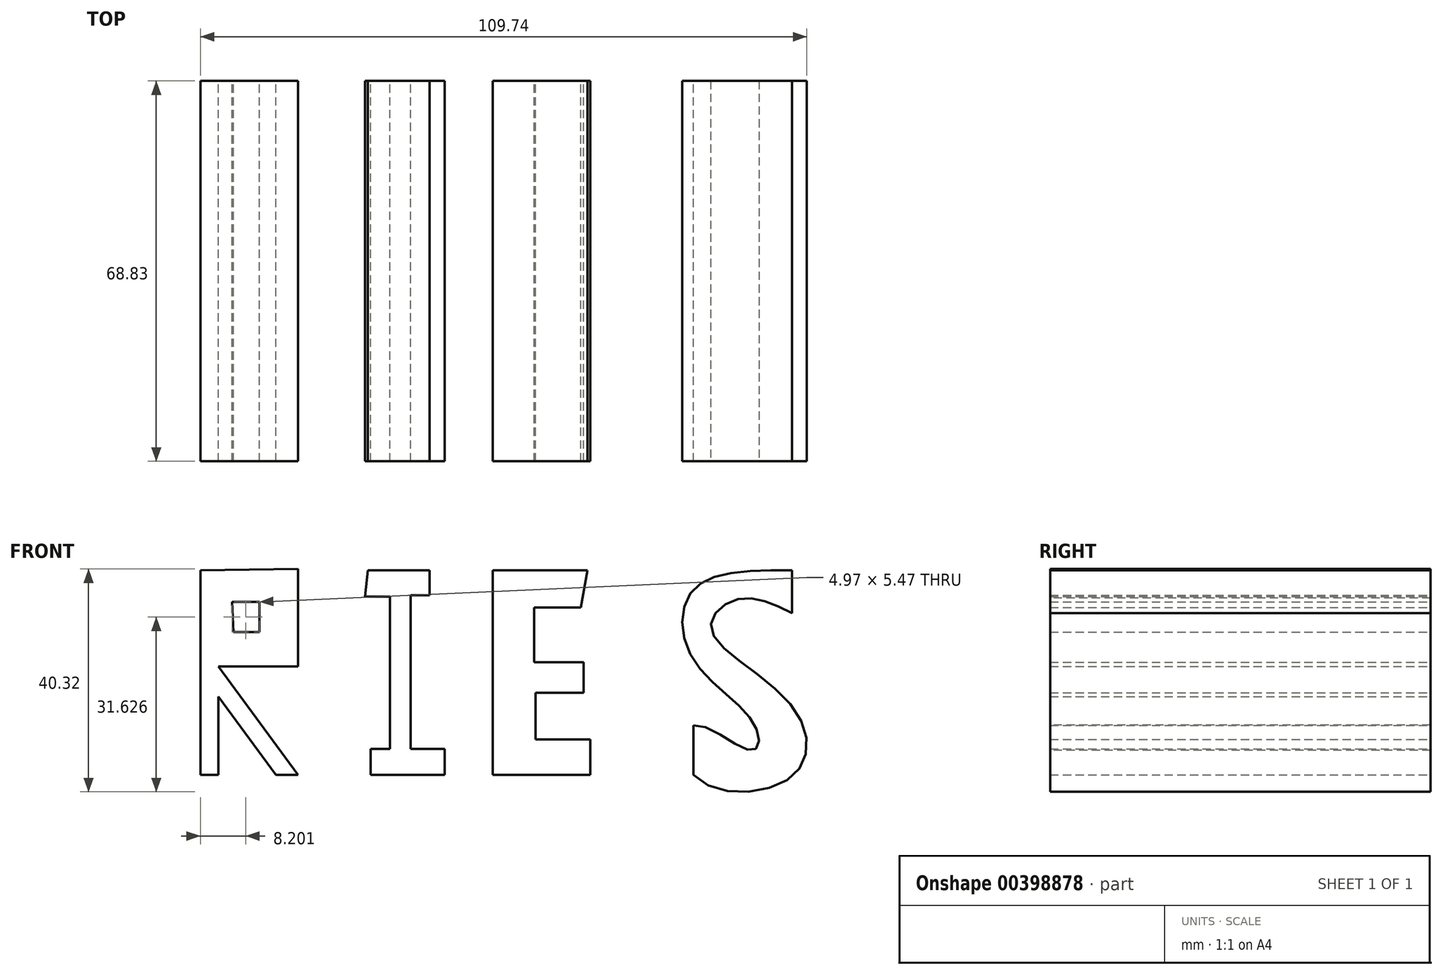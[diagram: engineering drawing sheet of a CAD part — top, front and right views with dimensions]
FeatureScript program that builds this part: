
annotation { "Feature Type Name" : "Feature", "Feature Type Description" : "" }
export const myFeature = defineFeature(function(context is Context, id is Id, definition is map)
    precondition{}
    {
        {
            var Q0;
            Q0=qCreatedBy(makeId("Front.planeOp"),FACE);
            var sketch = newSketch(context, id + "F0", { "sketchPlane" : qUnion([Q0])});
            skLineSegment(sketch, "E0", {"start": v(-44.23, 49.94) * mm, "end": v(-44.23, 12.92) * mm});
            skLineSegment(sketch, "E1", {"start": v(-44.23, 12.92) * mm, "end": v(-41, 12.92) * mm});
            skLineSegment(sketch, "E2", {"start": v(-41, 12.92) * mm, "end": v(-41, 27.08) * mm});
            skLineSegment(sketch, "E3", {"start": v(-41, 27.08) * mm, "end": v(-30.56, 12.92) * mm});
            skLineSegment(sketch, "E4", {"start": v(-30.56, 12.92) * mm, "end": v(-26.59, 12.92) * mm});
            skLineSegment(sketch, "E5", {"start": v(-26.59, 12.92) * mm, "end": v(-41, 32.55) * mm});
            skLineSegment(sketch, "E6", {"start": v(-41, 32.55) * mm, "end": v(-26.59, 32.55) * mm});
            skLineSegment(sketch, "E7", {"start": v(-26.59, 32.55) * mm, "end": v(-26.59, 50.2) * mm});
            skLineSegment(sketch, "E8", {"start": v(-26.59, 50.2) * mm, "end": v(-44.23, 49.94) * mm});
            skLineSegment(sketch, "E9", {"start": v(-13.91, 49.94) * mm, "end": v(-2.73, 49.94) * mm});
            skLineSegment(sketch, "E10", {"start": v(-2.73, 49.94) * mm, "end": v(-2.73, 45.47) * mm});
            skLineSegment(sketch, "E11", {"start": v(-2.73, 45.47) * mm, "end": v(-6.21, 45.47) * mm});
            skLineSegment(sketch, "E12", {"start": v(-6.21, 45.47) * mm, "end": v(-6.21, 17.64) * mm});
            skLineSegment(sketch, "E13", {"start": v(-6.21, 17.64) * mm, "end": v(0, 17.64) * mm});
            skLineSegment(sketch, "E14", {"start": v(0, 17.64) * mm, "end": v(0, 12.92) * mm});
            skLineSegment(sketch, "E15", {"start": v(0, 12.92) * mm, "end": v(-13.42, 12.92) * mm});
            skLineSegment(sketch, "E16", {"start": v(-13.42, 12.92) * mm, "end": v(-13.42, 17.64) * mm});
            skLineSegment(sketch, "E17", {"start": v(-13.42, 17.64) * mm, "end": v(-9.94, 17.64) * mm});
            skLineSegment(sketch, "E18", {"start": v(-9.94, 17.64) * mm, "end": v(-9.94, 45.22) * mm});
            skLineSegment(sketch, "E19", {"start": v(-9.94, 45.22) * mm, "end": v(-14.41, 45.22) * mm});
            skLineSegment(sketch, "E20", {"start": v(-14.41, 45.22) * mm, "end": v(-13.91, 49.94) * mm});
            skLineSegment(sketch, "E21", {"start": v(25.84, 49.94) * mm, "end": v(8.7, 49.94) * mm});
            skLineSegment(sketch, "E22", {"start": v(8.7, 49.94) * mm, "end": v(8.7, 12.92) * mm});
            skLineSegment(sketch, "E23", {"start": v(8.7, 12.92) * mm, "end": v(26.34, 12.92) * mm});
            skLineSegment(sketch, "E24", {"start": v(26.34, 12.92) * mm, "end": v(26.34, 19.38) * mm});
            skLineSegment(sketch, "E25", {"start": v(26.34, 19.38) * mm, "end": v(16.4, 19.38) * mm});
            skLineSegment(sketch, "E26", {"start": v(16.4, 19.38) * mm, "end": v(16.4, 27.83) * mm});
            skLineSegment(sketch, "E27", {"start": v(16.4, 27.83) * mm, "end": v(25.1, 27.83) * mm});
            skLineSegment(sketch, "E28", {"start": v(25.1, 27.83) * mm, "end": v(25.1, 33.3) * mm});
            skLineSegment(sketch, "E29", {"start": v(25.1, 33.3) * mm, "end": v(16.15, 33.3) * mm});
            skLineSegment(sketch, "E30", {"start": v(16.15, 33.3) * mm, "end": v(16.15, 43.24) * mm});
            skLineSegment(sketch, "E31", {"start": v(16.15, 43.24) * mm, "end": v(24.6, 43.24) * mm});
            skLineSegment(sketch, "E32", {"start": v(24.6, 43.24) * mm, "end": v(25.84, 49.94) * mm});
            skLineSegment(sketch, "E33", {"start": v(62.87, 49.94) * mm, "end": v(62.87, 42.24) * mm});
            skLineSegment(sketch, "E34", {"start": v(44.97, 21.87) * mm, "end": v(44.97, 12.92) * mm});
            skPoint(sketch, "E35.7.internal.snap0", {"position": v(44.97, 17.4) * mm});
            skFitSpline(sketch, "E35", {"points": [v(62.87, 42.24) * mm, v(52.93, 44.73) * mm, v(48.2, 39.26) * mm, v(62.87, 25.34) * mm, v(62.87, 12.67) * mm, v(44.97, 12.92) * mm, v(44.97, 21.87) * mm, v(55.66, 17.4) * mm, v(56.16, 21.87) * mm, v(44.97, 33.8) * mm, v(44.97, 46.47) * mm, v(62.87, 49.94) * mm], "startDerivative": vector(-121.9, 59.13) * mm, "endDerivative": vector(198.23, -1.14) * mm});
            skLineSegment(sketch, "E36", {"start": v(-38.51, 44.23) * mm, "end": v(-33.54, 44.23) * mm});
            skLineSegment(sketch, "E37", {"start": v(-33.54, 44.23) * mm, "end": v(-33.54, 38.76) * mm});
            skLineSegment(sketch, "E38", {"start": v(-33.54, 38.76) * mm, "end": v(-38.27, 38.76) * mm});
            skLineSegment(sketch, "E39", {"start": v(-38.27, 38.76) * mm, "end": v(-38.51, 44.23) * mm});
            skSolve(sketch);
        }
        {
            var Q0;
            Q0=makeQuery(id+"F0.imprint","IMPRINT",FACE,{"disambiguationData":[TD([[makeQuery(id+"F0.imprint","IMPRINT",EDGE,{"derivedFrom":sQuery(id+"F0.wireOp",EDGE,"E0")}),1.0]])]});
            var Q1;
            Q1=makeQuery(id+"F0.imprint","IMPRINT",FACE,{"disambiguationData":[TD([[makeQuery(id+"F0.imprint","IMPRINT",EDGE,{"derivedFrom":sQuery(id+"F0.wireOp",EDGE,"E9")}),-1.0]])]});
            var Q2;
            Q2=makeQuery(id+"F0.imprint","IMPRINT",FACE,{"disambiguationData":[TD([[makeQuery(id+"F0.imprint","IMPRINT",EDGE,{"derivedFrom":sQuery(id+"F0.wireOp",EDGE,"E21")}),1.0]])]});
            var Q3;
            {var subQ0=sQuery(id+"F0.wireOp",EDGE,"E33");Q3=makeQuery(id+"F0.imprint","IMPRINT",FACE,{"disambiguationData":[TD([[makeQuery(id+"F0.imprint","IMPRINT",EDGE,{"derivedFrom":subQ0}),-1.0]])]});}
            extrude(context, id + "F1", {"entities" : qUnion([Q0, Q1, Q2, Q3]), "depth" : 68.83 * mm});
        }
    });
